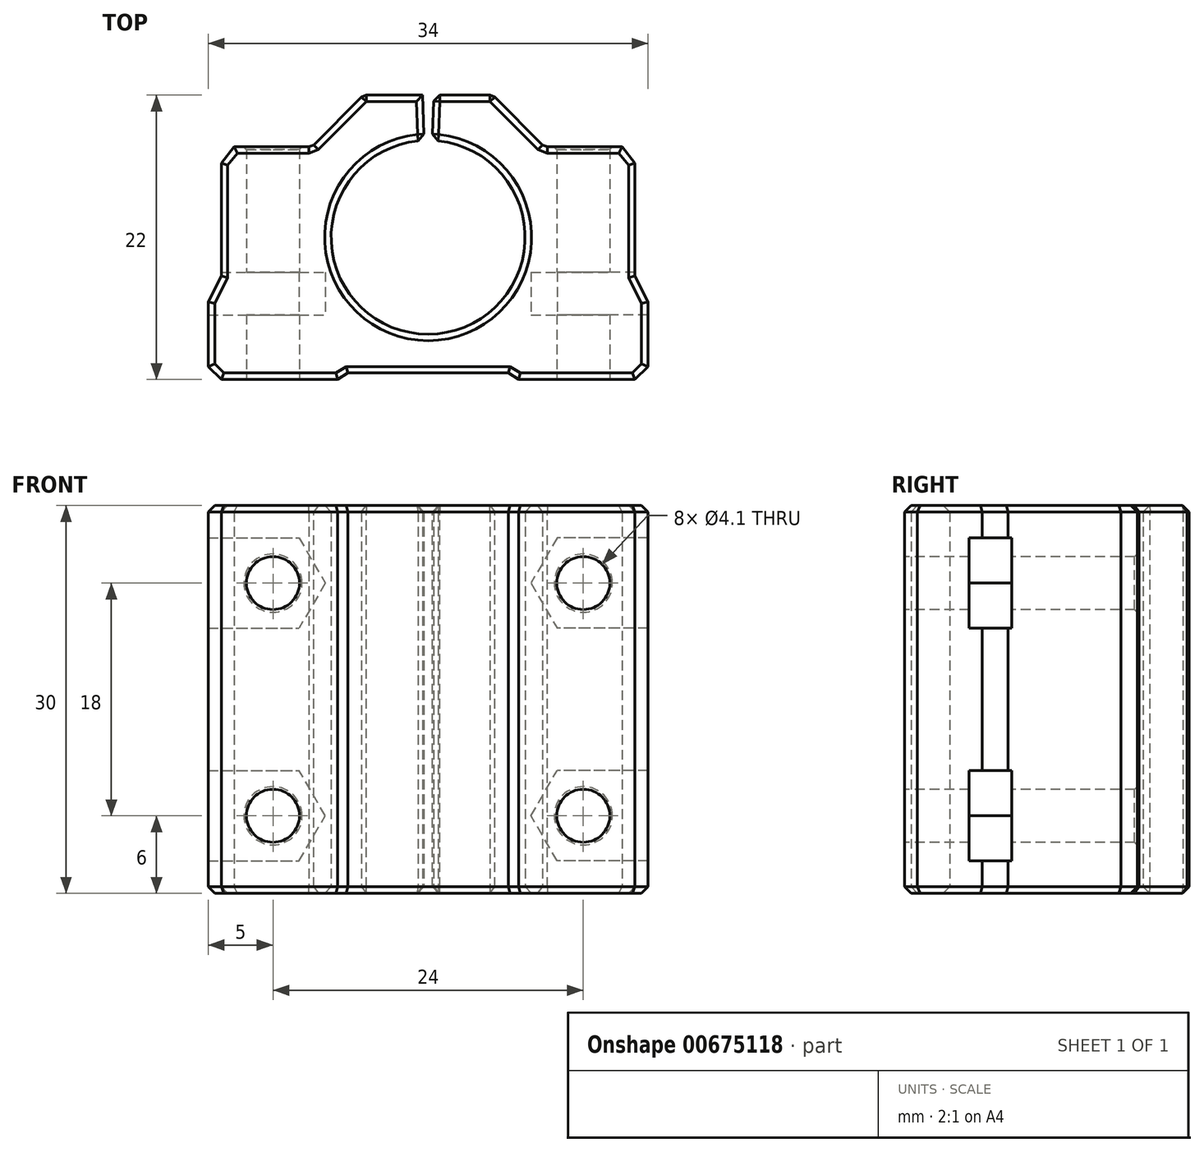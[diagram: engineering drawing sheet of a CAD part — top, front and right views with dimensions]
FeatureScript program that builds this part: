
annotation { "Feature Type Name" : "Feature", "Feature Type Description" : "" }
export const myFeature = defineFeature(function(context is Context, id is Id, definition is map)
    precondition{}
    {
        {
            var Q0;
            Q0=qCreatedBy(makeId("Top.planeOp"),FACE);
            var sketch = newSketch(context, id + "F0", { "sketchPlane" : qUnion([Q0])});
            skLineSegment(sketch, "E0", {"start": v(16, -11) * mm, "end": v(17, -10) * mm});
            skLineSegment(sketch, "E1", {"start": v(17, -10) * mm, "end": v(17, -5) * mm});
            skLineSegment(sketch, "E2", {"start": v(17, -5) * mm, "end": v(16, -3) * mm});
            skLineSegment(sketch, "E3", {"start": v(16, -3) * mm, "end": v(16, 5.75) * mm});
            skLineSegment(sketch, "E4", {"start": v(16, 5.75) * mm, "end": v(15, 7) * mm});
            skLineSegment(sketch, "E5", {"start": v(15, 7) * mm, "end": v(9, 7) * mm});
            skLineSegment(sketch, "E6", {"start": v(9, 7) * mm, "end": v(5, 11) * mm});
            skLineSegment(sketch, "E7", {"start": v(5, 11) * mm, "end": v(0.44, 11) * mm});
            skLineSegment(sketch, "E8", {"start": v(-5, 11) * mm, "end": v(-9, 7) * mm});
            skLineSegment(sketch, "E9", {"start": v(-9, 7) * mm, "end": v(-15, 7) * mm});
            skLineSegment(sketch, "E10", {"start": v(-15, 7) * mm, "end": v(-16, 5.75) * mm});
            skLineSegment(sketch, "E11", {"start": v(-16, 5.75) * mm, "end": v(-16, -3) * mm});
            skLineSegment(sketch, "E12", {"start": v(-16, -3) * mm, "end": v(-17, -5) * mm});
            skLineSegment(sketch, "E13", {"start": v(-17, -5) * mm, "end": v(-17, -10) * mm});
            skLineSegment(sketch, "E14", {"start": v(-17, -10) * mm, "end": v(-16, -11) * mm});
            skArc(sketch, "E15", {"start": v(-0.3, 7.5) * mm, "mid": v(0, -7.5) * mm, "end": v(0.3, 7.5) * mm});
            skLineSegment(sketch, "E16", {"start": v(-16, -11) * mm, "end": v(-7, -11) * mm});
            skLineSegment(sketch, "E17", {"start": v(-7, -11) * mm, "end": v(-6.2, -10.5) * mm});
            skLineSegment(sketch, "E18", {"start": v(-6.2, -10.5) * mm, "end": v(6.2, -10.5) * mm});
            skLineSegment(sketch, "E19", {"start": v(6.2, -10.5) * mm, "end": v(7, -11) * mm});
            skLineSegment(sketch, "E20", {"start": v(7, -11) * mm, "end": v(16, -11) * mm});
            skLineSegment(sketch, "E21", {"start": v(-0.44, 11) * mm, "end": v(-0.3, 7.5) * mm});
            skLineSegment(sketch, "E22", {"start": v(0.3, 7.5) * mm, "end": v(0.44, 11) * mm});
            skLineSegment(sketch, "E23.trimOffspring", {"start": v(-0.44, 11) * mm, "end": v(-5, 11) * mm});
            skSolve(sketch);
        }
        {
            var Q0;
            Q0=qSketchRegion(id+"F0",true);
            extrude(context, id + "F1", {"entities" : qUnion([Q0]), "depth" : 15 * mm, "offsetDistance" : 25 * mm, "hasSecondDirection" : true, "secondDirectionOppositeDirection" : true, "secondDirectionDepth" : 15 * mm});
        }
        {
            var Q0;
            Q0=makeQuery(id+"F1.opExtrude","SWEPT_FACE",FACE,{"disambiguationData":[OSD([sQuery(id+"F0.wireOp",EDGE,"E16")])]});
            var sketch = newSketch(context, id + "F2", { "sketchPlane" : qUnion([Q0])});
            skCircle(sketch, "E24", {"center": v(-12, 9) * mm, "radius": 2.05 * mm});
            skCircle(sketch, "E25", {"center": v(-12, -9) * mm, "radius": 2.05 * mm});
            skCircle(sketch, "E26", {"center": v(12, 9) * mm, "radius": 2.05 * mm});
            skCircle(sketch, "E27", {"center": v(12, -9) * mm, "radius": 2.05 * mm});
            skSolve(sketch);
        }
        {
            var Q0;
            Q0=makeQuery(id+"F2.imprint","IMPRINT",FACE,{"disambiguationData":[TD([[makeQuery(id+"F2.imprint","IMPRINT",EDGE,{"derivedFrom":sQuery(id+"F2.wireOp",EDGE,"E24")}),1.0]])]});
            var Q1;
            Q1=makeQuery(id+"F2.imprint","IMPRINT",FACE,{"disambiguationData":[TD([[makeQuery(id+"F2.imprint","IMPRINT",EDGE,{"derivedFrom":sQuery(id+"F2.wireOp",EDGE,"E26")}),1.0]])]});
            var Q2;
            Q2=makeQuery(id+"F2.imprint","IMPRINT",FACE,{"disambiguationData":[TD([[makeQuery(id+"F2.imprint","IMPRINT",EDGE,{"derivedFrom":sQuery(id+"F2.wireOp",EDGE,"E27")}),1.0]])]});
            var Q3;
            Q3=makeQuery(id+"F2.imprint","IMPRINT",FACE,{"disambiguationData":[TD([[makeQuery(id+"F2.imprint","IMPRINT",EDGE,{"derivedFrom":sQuery(id+"F2.wireOp",EDGE,"E25")}),1.0]])]});
            var Q4;
            Q4=sQuery(id+"F2.wireOp",EDGE,"E25");
            var Q5;
            Q5=sQuery(id+"F2.wireOp",EDGE,"E24");
            var Q6;
            Q6=sQuery(id+"F2.wireOp",EDGE,"E26");
            var Q7;
            Q7=sQuery(id+"F2.wireOp",EDGE,"E27");
            extrude(context, id + "F3", {"entities" : qUnion([Q0, Q1, Q2, Q3]), "operationType" : NewBodyOperationType.REMOVE, "surfaceEntities" : qUnion([Q4, Q5, Q6, Q7]), "oppositeDirection" : true, "depth" : 25 * mm, "offsetDistance" : 25 * mm});
        }
        {
            var Q0;
            Q0=makeQuery(id+"F1.opExtrude","CAP_FACE",FACE,{"disambiguationData":[OSD([sQuery(id+"F0.wireOp",EDGE,"E0"),sQuery(id+"F0.wireOp",EDGE,"E1"),sQuery(id+"F0.wireOp",EDGE,"E2"),sQuery(id+"F0.wireOp",EDGE,"E3"),sQuery(id+"F0.wireOp",EDGE,"E4"),sQuery(id+"F0.wireOp",EDGE,"E5"),sQuery(id+"F0.wireOp",EDGE,"E6"),sQuery(id+"F0.wireOp",EDGE,"E7"),sQuery(id+"F0.wireOp",EDGE,"E8"),sQuery(id+"F0.wireOp",EDGE,"E9"),sQuery(id+"F0.wireOp",EDGE,"E10"),sQuery(id+"F0.wireOp",EDGE,"E11"),sQuery(id+"F0.wireOp",EDGE,"E12"),sQuery(id+"F0.wireOp",EDGE,"E13"),sQuery(id+"F0.wireOp",EDGE,"E14"),sQuery(id+"F0.wireOp",EDGE,"E15"),sQuery(id+"F0.wireOp",EDGE,"E16"),sQuery(id+"F0.wireOp",EDGE,"E17"),sQuery(id+"F0.wireOp",EDGE,"E18"),sQuery(id+"F0.wireOp",EDGE,"E19"),sQuery(id+"F0.wireOp",EDGE,"E20")])],"isStart":false});
            var Q1;
            {var subQ0=sQuery(id+"F0.wireOp",EDGE,"E15");Q1=makeQuery(id+"F6uso4rrdqJ6QKG_1.boolean.opBoolean","MERGE",FACE,{"derivedFrom":[makeQuery(id+"F1.opExtrude","CAP_FACE",FACE,{"disambiguationData":[OSD([sQuery(id+"F0.wireOp",EDGE,"E0"),sQuery(id+"F0.wireOp",EDGE,"E1"),sQuery(id+"F0.wireOp",EDGE,"E2"),sQuery(id+"F0.wireOp",EDGE,"E3"),sQuery(id+"F0.wireOp",EDGE,"E4"),sQuery(id+"F0.wireOp",EDGE,"E5"),sQuery(id+"F0.wireOp",EDGE,"E6"),sQuery(id+"F0.wireOp",EDGE,"E7"),sQuery(id+"F0.wireOp",EDGE,"E8"),sQuery(id+"F0.wireOp",EDGE,"E9"),sQuery(id+"F0.wireOp",EDGE,"E10"),sQuery(id+"F0.wireOp",EDGE,"E11"),sQuery(id+"F0.wireOp",EDGE,"E12"),sQuery(id+"F0.wireOp",EDGE,"E13"),sQuery(id+"F0.wireOp",EDGE,"E14"),subQ0,sQuery(id+"F0.wireOp",EDGE,"E16"),sQuery(id+"F0.wireOp",EDGE,"E17"),sQuery(id+"F0.wireOp",EDGE,"E18"),sQuery(id+"F0.wireOp",EDGE,"E19"),sQuery(id+"F0.wireOp",EDGE,"E20")])],"isStart":true}),makeQuery(id+"F6uso4rrdqJ6QKG_1.opExtrude","CAP_FACE",FACE,{"disambiguationData":[OSD([subQ0,sQuery(id+"FfyqX5YnEJJNRPU_1.wireOp",EDGE,"Up2EdMFq-rjqs-rVvq-JJag-18Bq9Nor02xC")])],"isStart":true})]});}
            var Q2;
            Q2=makeQuery(id+"F1.opExtrude","SWEPT_EDGE",EDGE,{"disambiguationData":[OSD([sQuery(id+"F0.wireOp",EDGE,"E8"),sQuery(id+"F0.wireOp",EDGE,"E9")])]});
            var Q3;
            Q3=makeQuery(id+"F1.opExtrude","SWEPT_EDGE",EDGE,{"disambiguationData":[OSD([sQuery(id+"F0.wireOp",EDGE,"E7"),sQuery(id+"F0.wireOp",EDGE,"E8")])]});
            var Q4;
            Q4=makeQuery(id+"F1.opExtrude","SWEPT_EDGE",EDGE,{"disambiguationData":[OSD([sQuery(id+"F0.wireOp",EDGE,"E6"),sQuery(id+"F0.wireOp",EDGE,"E7")])]});
            var Q5;
            Q5=makeQuery(id+"F1.opExtrude","SWEPT_EDGE",EDGE,{"disambiguationData":[OSD([sQuery(id+"F0.wireOp",EDGE,"E5"),sQuery(id+"F0.wireOp",EDGE,"E6")])]});
            var Q6;
            Q6=makeQuery(id+"F1.opExtrude","SWEPT_EDGE",EDGE,{"disambiguationData":[OSD([sQuery(id+"F0.wireOp",EDGE,"E15"),sQuery(id+"F0.wireOp",EDGE,"E22")])]});
            var Q7;
            Q7=makeQuery(id+"F1.opExtrude","SWEPT_EDGE",EDGE,{"disambiguationData":[OSD([sQuery(id+"F0.wireOp",EDGE,"E15"),sQuery(id+"F0.wireOp",EDGE,"E21")])]});
            chamfer(context, id + "F4", {"entities" : qUnion([Q0, Q1, Q2, Q3, Q4, Q5, Q6, Q7]), "width" : .5 * mm, "tangentPropagation" : true});
        }
        {
            var Q0;
            Q0=makeQuery(id+"F1.opExtrude","SWEPT_FACE",FACE,{"disambiguationData":[OSD([sQuery(id+"F0.wireOp",EDGE,"E16")])]});
            cPlane(context, id + "F5", {"entities" : qUnion([Q0]), "cplaneType" : CPlaneType.OFFSET, "offset" : 5 * mm, "oppositeDirection" : true, "width" : 150 * mm, "height" : 150 * mm});
        }
        {
            var Q0;
            Q0=qCreatedBy(id+"F5.planeOp",FACE);
            var sketch = newSketch(context, id + "F6", { "sketchPlane" : qUnion([Q0])});
            skCircle(sketch, "E28.0", {"center": v(-12, 9) * mm, "radius": 2.05 * mm});
            skCircle(sketch, "E29.cCircle", {"center": v(-12, 9) * mm, "radius": 3.5 * mm, "construction": true});
            skLineSegment(sketch, "E29.1", {"start": v(-9.98, 12.5) * mm, "end": v(-7.96, 9) * mm});
            skLineSegment(sketch, "E29.2", {"start": v(-7.96, 9) * mm, "end": v(-9.98, 5.5) * mm});
            skPoint(sketch, "E29.0.midPoint", {"position": v(-12, 12.5) * mm});
            skLineSegment(sketch, "E30.0.0", {"start": v(-17, 14.5) * mm, "end": v(-17, -14.5) * mm});
            skLineSegment(sketch, "E30.0.2", {"start": v(-17, -14.5) * mm, "end": v(-17, 14.5) * mm});
            skLineSegment(sketch, "E31.bottom", {"start": v(-17, 12.5) * mm, "end": v(-9.98, 12.5) * mm});
            skLineSegment(sketch, "E31.top", {"start": v(-17, 5.5) * mm, "end": v(-9.98, 5.5) * mm});
            skLineSegment(sketch, "E31.left", {"start": v(-17, 12.5) * mm, "end": v(-17, 5.5) * mm});
            skLineSegment(sketch, "E32.MirrorCS", {"start": v(7.96, 9) * mm, "end": v(9.98, 5.5) * mm});
            skLineSegment(sketch, "E33.MirrorCS", {"start": v(17, 12.5) * mm, "end": v(17, 5.5) * mm});
            skPoint(sketch, "E34.MirrorP", {"position": v(12, 12.5) * mm});
            skLineSegment(sketch, "E35.MirrorCS", {"start": v(9.98, 12.5) * mm, "end": v(7.96, 9) * mm});
            skCircle(sketch, "E36.MirrorC", {"center": v(12, 9) * mm, "radius": 3.5 * mm, "construction": true});
            skLineSegment(sketch, "E37.MirrorCS", {"start": v(17, 5.5) * mm, "end": v(9.98, 5.5) * mm});
            skLineSegment(sketch, "E38.MirrorCS", {"start": v(17, 12.5) * mm, "end": v(9.98, 12.5) * mm});
            skCircle(sketch, "E39.MirrorC", {"center": v(12, 9) * mm, "radius": 2.05 * mm});
            skLineSegment(sketch, "E40.MirrorCS", {"start": v(17, 14.5) * mm, "end": v(17, -14.5) * mm});
            skLineSegment(sketch, "E41.MirrorCS", {"start": v(17, -14.5) * mm, "end": v(17, 14.5) * mm});
            skLineSegment(sketch, "E42.MirrorCS", {"start": v(9.98, -12.5) * mm, "end": v(7.96, -9) * mm});
            skLineSegment(sketch, "E43.MirrorCS", {"start": v(17, -12.5) * mm, "end": v(17, -5.5) * mm});
            skLineSegment(sketch, "E44.MirrorCS", {"start": v(-17, -5.5) * mm, "end": v(-9.98, -5.5) * mm});
            skLineSegment(sketch, "E45.MirrorCS", {"start": v(17, -12.5) * mm, "end": v(9.98, -12.5) * mm});
            skLineSegment(sketch, "E46.MirrorCS", {"start": v(-9.98, -12.5) * mm, "end": v(-7.96, -9) * mm});
            skCircle(sketch, "E47.MirrorC", {"center": v(12, -9) * mm, "radius": 3.5 * mm, "construction": true});
            skPoint(sketch, "E48.MirrorP", {"position": v(-12, -12.5) * mm});
            skCircle(sketch, "E49.MirrorC", {"center": v(-12, -9) * mm, "radius": 2.05 * mm});
            skLineSegment(sketch, "E50.MirrorCS", {"start": v(-17, -12.5) * mm, "end": v(-9.98, -12.5) * mm});
            skLineSegment(sketch, "E51.MirrorCS", {"start": v(-7.96, -9) * mm, "end": v(-9.98, -5.5) * mm});
            skLineSegment(sketch, "E52.MirrorCS", {"start": v(7.96, -9) * mm, "end": v(9.98, -5.5) * mm});
            skCircle(sketch, "E53.MirrorC", {"center": v(12, -9) * mm, "radius": 2.05 * mm});
            skCircle(sketch, "E54.MirrorC", {"center": v(-12, -9) * mm, "radius": 3.5 * mm, "construction": true});
            skLineSegment(sketch, "E55.MirrorCS", {"start": v(17, -5.5) * mm, "end": v(9.98, -5.5) * mm});
            skPoint(sketch, "E56.MirrorP", {"position": v(12, -12.5) * mm});
            skLineSegment(sketch, "E57.MirrorCS", {"start": v(-17, -12.5) * mm, "end": v(-17, -5.5) * mm});
            skSolve(sketch);
        }
        {
            var Q0;
            Q0 = qSketchRegion(id + "F6", true);
            extrude(context, id + "F7", {"entities" : qUnion([Q0]), "operationType" : NewBodyOperationType.REMOVE, "oppositeDirection" : true, "depth" : 3.3 * mm, "offsetDistance" : 25 * mm});
        }
        {
            var Q0;
            Q0=makeQuery(id+"F3.boolean.opBoolean","INTERSECT",EDGE,{"derivedFrom":[makeQuery(id+"F1.opExtrude","SWEPT_FACE",FACE,{"disambiguationData":[OSD([sQuery(id+"F0.wireOp",EDGE,"E9")])]}),makeQuery(id+"F3.opExtrude","SWEPT_FACE",FACE,{"disambiguationData":[OSD([sQuery(id+"F2.wireOp",EDGE,"E24")])]})]});
            var Q1;
            Q1=makeQuery(id+"F3.boolean.opBoolean","INTERSECT",EDGE,{"derivedFrom":[makeQuery(id+"F1.opExtrude","SWEPT_FACE",FACE,{"disambiguationData":[OSD([sQuery(id+"F0.wireOp",EDGE,"E9")])]}),makeQuery(id+"F3.opExtrude","SWEPT_FACE",FACE,{"disambiguationData":[OSD([sQuery(id+"F2.wireOp",EDGE,"E25")])]})]});
            var Q2;
            Q2=makeQuery(id+"F3.boolean.opBoolean","INTERSECT",EDGE,{"derivedFrom":[makeQuery(id+"F1.opExtrude","SWEPT_FACE",FACE,{"disambiguationData":[OSD([sQuery(id+"F0.wireOp",EDGE,"E5")])]}),makeQuery(id+"F3.opExtrude","SWEPT_FACE",FACE,{"disambiguationData":[OSD([sQuery(id+"F2.wireOp",EDGE,"E27")])]})]});
            var Q3;
            Q3=makeQuery(id+"F3.boolean.opBoolean","INTERSECT",EDGE,{"derivedFrom":[makeQuery(id+"F1.opExtrude","SWEPT_FACE",FACE,{"disambiguationData":[OSD([sQuery(id+"F0.wireOp",EDGE,"E5")])]}),makeQuery(id+"F3.opExtrude","SWEPT_FACE",FACE,{"disambiguationData":[OSD([sQuery(id+"F2.wireOp",EDGE,"E26")])]})]});
            var Q4;
            Q4=makeQuery(id+"F3.boolean.opBoolean","COPY",EDGE,{"derivedFrom":makeQuery(id+"F3.opExtrude","CAP_EDGE",EDGE,{"disambiguationData":[OSD([sQuery(id+"F2.wireOp",EDGE,"E24")])],"isStart":true})});
            var Q5;
            Q5=makeQuery(id+"F3.boolean.opBoolean","COPY",EDGE,{"derivedFrom":makeQuery(id+"F3.opExtrude","CAP_EDGE",EDGE,{"disambiguationData":[OSD([sQuery(id+"F2.wireOp",EDGE,"E25")])],"isStart":true})});
            var Q6;
            Q6=makeQuery(id+"F3.boolean.opBoolean","COPY",EDGE,{"derivedFrom":makeQuery(id+"F3.opExtrude","CAP_EDGE",EDGE,{"disambiguationData":[OSD([sQuery(id+"F2.wireOp",EDGE,"E27")])],"isStart":true})});
            var Q7;
            Q7=makeQuery(id+"F3.boolean.opBoolean","COPY",EDGE,{"derivedFrom":makeQuery(id+"F3.opExtrude","CAP_EDGE",EDGE,{"disambiguationData":[OSD([sQuery(id+"F2.wireOp",EDGE,"E26")])],"isStart":true})});
            chamfer(context, id + "F8", {"entities" : qUnion([Q0, Q1, Q2, Q3, Q4, Q5, Q6, Q7]), "width" : .2 * mm, "tangentPropagation" : true});
        }
    });
